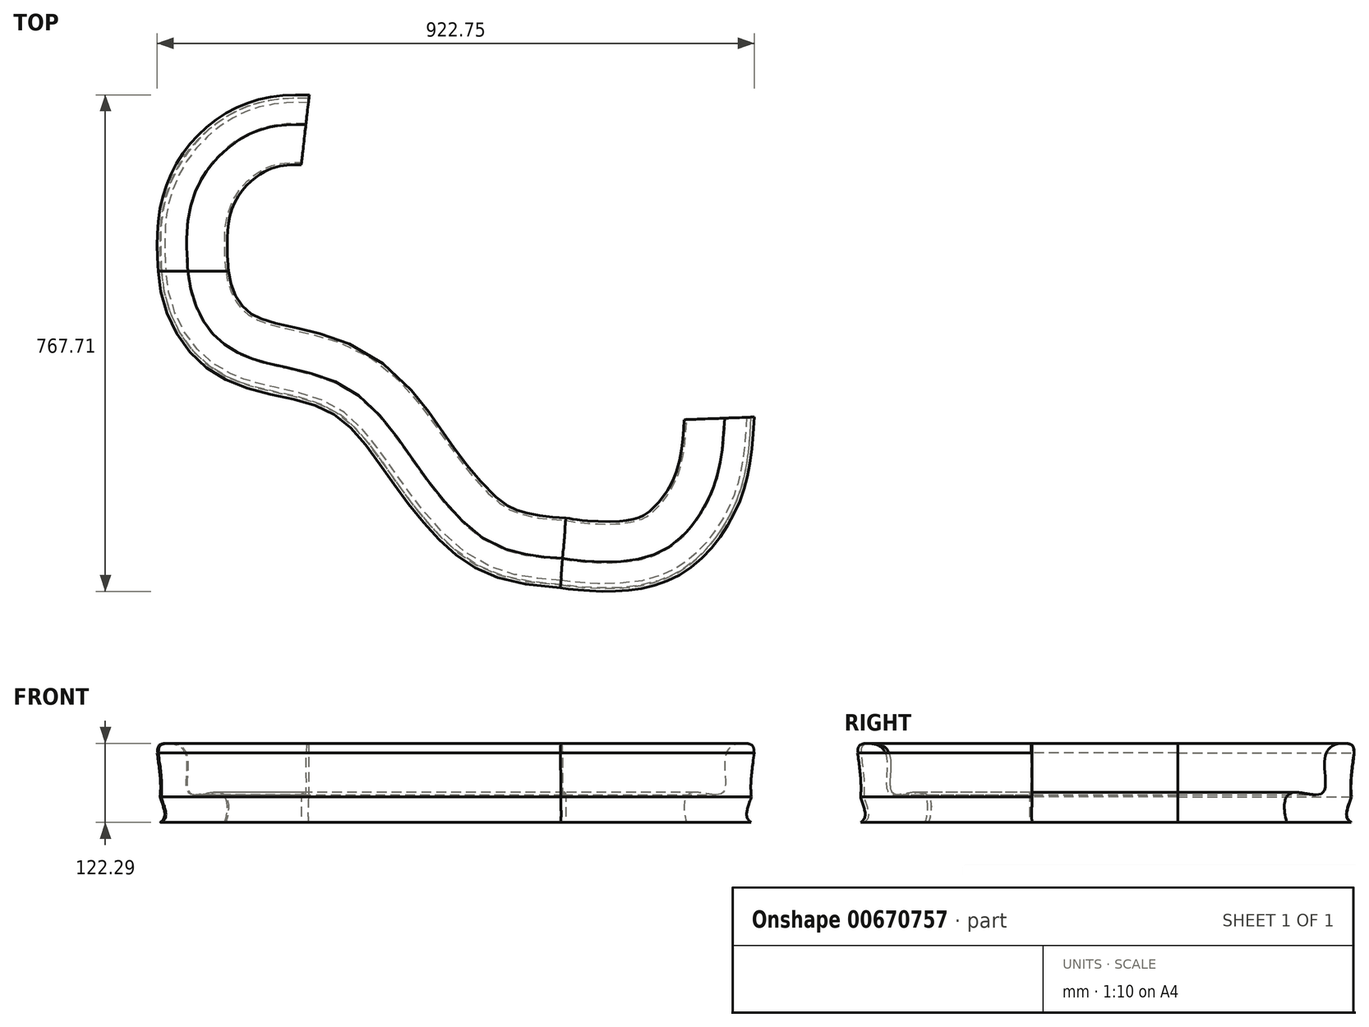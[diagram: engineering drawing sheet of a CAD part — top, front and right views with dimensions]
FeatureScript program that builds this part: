
annotation { "Feature Type Name" : "Feature", "Feature Type Description" : "" }
export const myFeature = defineFeature(function(context is Context, id is Id, definition is map)
    precondition{}
    {
        {
            var Q0;
            Q0=qCreatedBy(makeId("Front.planeOp"),FACE);
            var sketch = newSketch(context, id + "F0", { "sketchPlane" : qUnion([Q0])});
            skLineSegment(sketch, "E0.bottom", {"start": v(50, -60.1) * mm, "end": v(-49.75, -59.7) * mm});
            skPoint(sketch, "E0.middle", {"position": v(0, 0) * mm});
            skFitSpline(sketch, "E1", {"points": [v(-49.75, -59.7) * mm, v(-50.04, -20.18) * mm, v(-54.5, 47.27) * mm, v(-50, 60.1) * mm, v(-25.02, 60.11) * mm, v(-12.32, 49.08) * mm, v(-8.85, 23) * mm, v(-7.1, -12.8) * mm, v(13.84, -16.49) * mm, v(38.65, -13.56) * mm, v(50.15, -19.99) * mm, v(50, -60.1) * mm], "startDerivative": vector(366.44, 234.15) * mm, "endDerivative": vector(-149.72, -516.35) * mm});
            skPoint(sketch, "E0.top.start.orphan", {"position": v(49.75, 59.7) * mm});
            skPoint(sketch, "E2.3.internal.orphan", {"position": v(-65.37, 47.27) * mm});
            skFitSpline(sketch, "E3", {"points": [v(-49.75, -59.7) * mm, v(-50.04, -20.18) * mm, v(-54.5, 47.27) * mm], "startDerivative": vector(-41.48, 58.59) * mm, "endDerivative": vector(-21.35, 163.04) * mm});
            skSolve(sketch);
        }
        {
            var Q0;
            Q0=qCreatedBy(makeId("Top.planeOp"),FACE);
            var sketch = newSketch(context, id + "F1", { "sketchPlane" : qUnion([Q0])});
            skFitSpline(sketch, "E4", {"points": [v(-38.8, 0) * mm, v(-5.7, -99.67) * mm, v(83.4, -164.34) * mm, v(220.22, -204.92) * mm, v(318.99, -315.13) * mm, v(408.62, -420.34) * mm, v(568.39, -473.6) * mm], "startDerivative": vector(20.13, -621.91) * mm, "endDerivative": vector(1358.18, -62.69) * mm});
            skSolve(sketch);
        }
        {
            var Q0;
            Q0=makeQuery(id+"F0.imprint","IMPRINT",FACE,{"disambiguationData":[TD([[makeQuery(id+"F0.imprint","IMPRINT",EDGE,{"derivedFrom":sQuery(id+"F0.wireOp",EDGE,"E0.bottom")}),-1.0]])]});
            var Q1;
            Q1=sQuery(id+"F1.wireOp",EDGE,"E4");
            sweep(context, id + "F2", {"profiles" : qUnion([Q0]), "path" : qUnion([Q1])});
        }
        {
            var Q0;
            Q0=qCreatedBy(makeId("Top.planeOp"),FACE);
            var sketch = newSketch(context, id + "F3", { "sketchPlane" : qUnion([Q0])});
            skPoint(sketch, "E5.start.orphan", {"position": v(-35, 0) * mm});
            skFitSpline(sketch, "E6", {"points": [v(-35, 0) * mm, v(-35, 78.45) * mm, v(0, 172.25) * mm, v(72.49, 234.56) * mm, v(176.56, 253.04) * mm], "startDerivative": vector(-10.78, 165) * mm, "endDerivative": vector(474.33, -23.33) * mm});
            skSolve(sketch);
        }
        {
            var Q0;
            Q0=makeQuery(id+"F2.opSweep","CAP_FACE",FACE,{"disambiguationData":[OSD([sQuery(id+"F0.wireOp",EDGE,"E0.bottom"),sQuery(id+"F0.wireOp",EDGE,"E1"),sQuery(id+"F0.wireOp",EDGE,"E3"),sQuery(id+"F1.wireOp",VERTEX,"E4.start")])],"isStart":true});
            var Q1;
            Q1=sQuery(id+"F3.wireOp",EDGE,"E6");
            sweep(context, id + "F4", {"operationType" : NewBodyOperationType.ADD, "profiles" : qUnion([Q0]), "path" : qUnion([Q1])});
        }
        {
            var Q0;
            Q0=qCreatedBy(makeId("Top.planeOp"),FACE);
            var sketch = newSketch(context, id + "F5", { "sketchPlane" : qUnion([Q0])});
            skFitSpline(sketch, "E7", {"points": [v(568.17, -469.5) * mm, v(647.58, -475.08) * mm, v(749.93, -447.19) * mm, v(822.64, -356.16) * mm, v(846.83, -226) * mm], "startDerivative": vector(213.43, -36.5) * mm, "endDerivative": vector(31.57, 627.24) * mm});
            skSolve(sketch);
        }
        {
            var Q0;
            Q0=makeQuery(id+"F2.opSweep","CAP_FACE",FACE,{"disambiguationData":[OSD([sQuery(id+"F0.wireOp",EDGE,"E0.bottom"),sQuery(id+"F0.wireOp",EDGE,"E1"),sQuery(id+"F0.wireOp",EDGE,"E3"),sQuery(id+"F1.wireOp",VERTEX,"E4.end")])],"isStart":false});
            var Q1;
            Q1 = qSketchRegion(id + "F5", true);
            var Q2;
            Q2=sQuery(id+"F5.wireOp",EDGE,"E7");
            sweep(context, id + "F6", {"operationType" : NewBodyOperationType.ADD, "profiles" : qUnion([Q0, Q1]), "path" : qUnion([Q2])});
        }
    });
